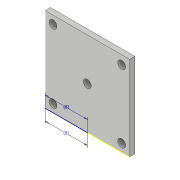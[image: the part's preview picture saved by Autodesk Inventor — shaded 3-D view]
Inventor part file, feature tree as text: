
AUTODESK INVENTOR PART (.ipt)
format: ipt  version: 2019 (Build 230136000, 136)  size: 113,664 bytes
history: native  units: in
note: dims shown in document units (in); Inventor stores cm internally (conversion verified against a paired STEP export)
features: sketch x4, extrude x3
ambient origin geometry x8: Origin, YZ Plane, XZ Plane, XY Plane, X Axis, Y Axis, Z Axis, Center Point
bodies: Solid1 (feature_tree)
feature tree (7):
  extrude  "Extrusion1"  Depth=6.2992in
  extrude  "Extrusion2"  Depth=0.3937in
  sketch  "Sketch3"  dims[d5=0.5906in d6=0.5906in]
  extrude  "Extrusion3"  Depth=0.5906in
  sketch  "Sketch1"  dims[d0=6.2992in d1=6.2992in]
  sketch  "Sketch2"  dims[d2=0.3937in d3=0.0in d4=0.5906in]
  sketch  "Sketch4"  dims[d7=0.5906in d8=0.5906in d9=0.6496in d10=0.5906in d11=0.5906in d12=0.5906in d13=0.5906in d14=0.5906in d15=0.5906in d16=0.3937in d17=0.0in d18=3.1496in d19=3.1496in d20=3.1496in d21=3.1496in d22=3.1496in d23=0.5906in d24=0.3937in d25=0.0in]
